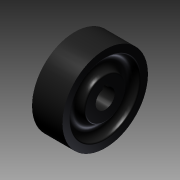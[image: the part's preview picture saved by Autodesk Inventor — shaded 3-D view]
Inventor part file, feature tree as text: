
AUTODESK INVENTOR PART (.ipt)
format: ipt  version: 2012 (Build 160160000, 160)  size: 188,928 bytes
history: native  units: in
note: dims shown in document units (in); Inventor stores cm internally (conversion verified against a paired STEP export)
features: sketch x2, revolve x1, fillet x1, extrude x1
ambient origin geometry x8: Origin, YZ Plane, XZ Plane, XY Plane, X Axis, Y Axis, Z Axis, Center Point
bodies: Solid1 (feature_tree)
feature tree (5):
  revolve  "Revolution1"  [1 undecoded]
  fillet  "Fillet1"  Radius=0.25in
  extrude  "Extrusion1"  Depth=0.1875in
  sketch  "Sketch1"  dims[d0=0.8in d1=0.875in d3=0.25in]
  sketch  "Sketch2"  dims[d4=0.4in d5=0.1875in d6=0.1875in d7=0.4in d8=90.0deg d9=0.0312in d10=0.125in d11=0.125in d12=0.0625in d13=0.5in d14=0.3125in d15=1.0in d16=0.0in]
note: 1 required parameter value undecoded (feature->parameter linkage not recoverable at this tier; creation-order binding heuristic only, values carry confidence <= 0.55)
